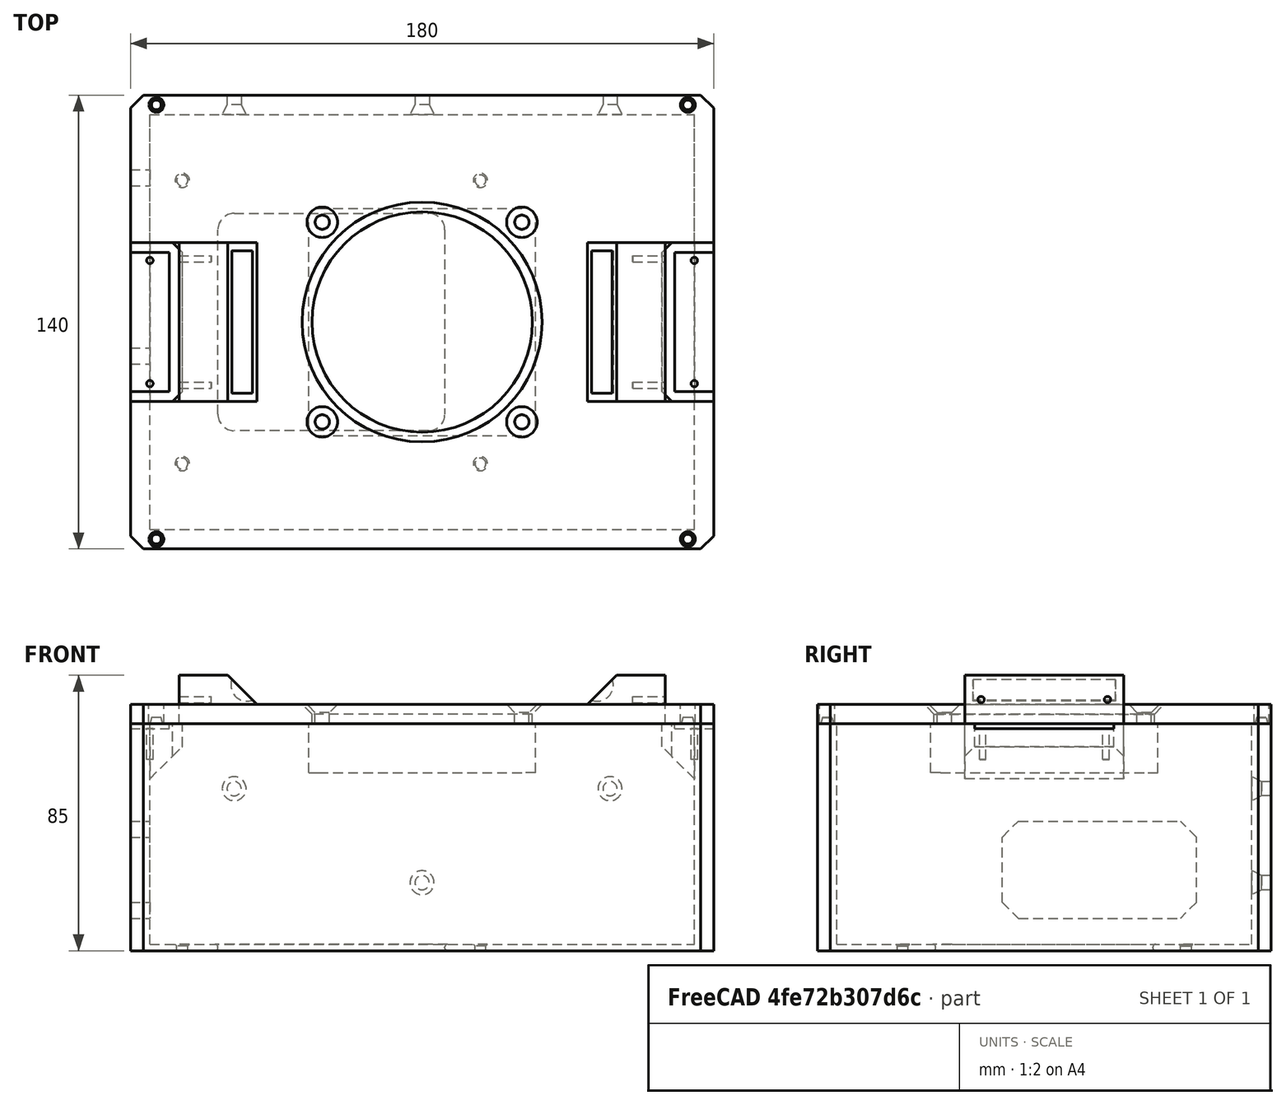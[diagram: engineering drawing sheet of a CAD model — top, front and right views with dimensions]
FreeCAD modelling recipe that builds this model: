
FCSTD DOCUMENT  (FreeCAD 0.19R24276 (Git))
Label: CajaElectronicaANETA8
License: All rights reserved
LicenseURL: http://en.wikipedia.org/wiki/All_rights_reserved
objects: Part::Cylinder×26, Part::MultiFuse×18, Part::Offset×15, TechDraw::DrawViewDimension×15, Part::Box×14, Part::Cut×13, Part::Chamfer×9, Part::Cone×7, Part::Fillet×3, TechDraw::DrawProjGroupItem×3, TechDraw::DrawSVGTemplate×2, TechDraw::DrawViewPart×2, TechDraw::DrawPage×2, TechDraw::DrawProjGroup×1, TechDraw::DrawViewAnnotation×1
note: 105 computed .brp shape members not serialized (recipe doc carries the construction recipe); baked Part::Feature solids carry a one-line shape summary decoded from their .brp

FEATURE [Part::Box] Box  label="Cubo"
  AttacherType = Attacher::AttachEngine3D
  Height = 70
  Length = 180
  Width = 140
FEATURE [Part::Box] Box001  label="Cubo001"
  AttacherType = Attacher::AttachEngine3D
  Height = 68
  Length = 168
  Placement = pos=(6,6,2) rot=(0,0,1;0rad)
  Width = 128
FEATURE [Part::Cut] Cut
  Base = -> Box
  Tool = -> Box001
FEATURE [Part::Cylinder] Cylinder  label="Cilindro"
  Angle = 360
  AttacherType = Attacher::AttachEngine3D
  Height = 2
  Placement = pos=(16,26.3,0) rot=(0,0,1;0rad)
  Radius = 1.5
FEATURE [Part::Cylinder] Cylinder001  label="Cilindro001"
  Angle = 360
  AttacherType = Attacher::AttachEngine3D
  Height = 2
  Placement = pos=(16,113.7,0) rot=(0,0,1;0rad)
  Radius = 1.5
FEATURE [Part::Cylinder] Cylinder002  label="Cilindro002"
  Angle = 360
  AttacherType = Attacher::AttachEngine3D
  Height = 2
  Placement = pos=(108,26.3,0) rot=(0,0,1;0rad)
  Radius = 1.5
FEATURE [Part::Cylinder] Cylinder003  label="Cilindro003"
  Angle = 360
  AttacherType = Attacher::AttachEngine3D
  Height = 2
  Placement = pos=(108,113.7,0) rot=(0,0,1;0rad)
  Radius = 1.5
FEATURE [Part::Chamfer] Chamfer
  Base = -> Cut
  Edges = 4 edges r=4: [Edge1,Edge3,Edge6,Edge15]
FEATURE [Part::Box] Box002  label="Cubo002"
  AttacherType = Attacher::AttachEngine3D
  Height = 2
  Length = 70
  Placement = pos=(27,36.5,0) rot=(0,0,1;0rad)
  Width = 67
FEATURE [Part::Fillet] Fillet
  Base = -> Box002
  Edges = 4 edges r=5: [Edge1,Edge3,Edge5,Edge7]
FEATURE [Part::Cut] Cut001
  Base = -> Chamfer
  Tool = -> Fillet
FEATURE [Part::Offset] Offset
  Fill = false
  Intersection = false
  Join = 0
  Mode = 0
  SelfIntersection = false
  Source = -> Cylinder
  Value = 0.2
FEATURE [Part::Offset] Offset001
  Fill = false
  Intersection = false
  Join = 0
  Mode = 0
  SelfIntersection = false
  Source = -> Cylinder001
  Value = 0.2
FEATURE [Part::Offset] Offset002
  Fill = false
  Intersection = false
  Join = 0
  Mode = 0
  SelfIntersection = false
  Source = -> Cylinder002
  Value = 0.2
FEATURE [Part::Offset] Offset003
  Fill = false
  Intersection = false
  Join = 0
  Mode = 0
  SelfIntersection = false
  Source = -> Cylinder003
  Value = 0.2
FEATURE [Part::MultiFuse] Fusion
  Shapes = -> [Offset,Offset001,Offset002,Offset003]
FEATURE [Part::Cut] Cut002
  Base = -> Cut001
  Tool = -> Fusion
FEATURE [Part::Chamfer] Chamfer001
  Base = -> Cut002
  Edges = 4 edges r=0.5: [Edge50,Edge52,Edge70,Edge72]
FEATURE [Part::Fillet] Fillet001
  Base = -> Chamfer001
  Edges = 2 edges r=0.9: [Edge17,Edge30]
FEATURE [Part::Cylinder] Cylinder004  label="Cilindro004"
  Angle = 360
  AttacherType = Attacher::AttachEngine3D
  Height = 6
  Placement = pos=(32,140,50) rot=(1,0,0;1.5708rad)
  Radius = 2
FEATURE [Part::Cylinder] Cylinder005  label="Cilindro005"
  Angle = 360
  AttacherType = Attacher::AttachEngine3D
  Height = 6
  Placement = pos=(148,140,50) rot=(1,0,0;1.5708rad)
  Radius = 2
FEATURE [Part::Cylinder] Cylinder006  label="Cilindro006"
  Angle = 360
  AttacherType = Attacher::AttachEngine3D
  Height = 6
  Placement = pos=(90,140,21) rot=(1,0,0;1.5708rad)
  Radius = 2
FEATURE [Part::Cone] Cone  label="Cono"
  Angle = 360
  AttacherType = Attacher::AttachEngine3D
  Height = 3
  Placement = pos=(90,137,21) rot=(1,0,0;1.5708rad)
  Radius1 = 2
  Radius2 = 3.5
FEATURE [Part::Cone] Cone001  label="Cono001"
  Angle = 360
  AttacherType = Attacher::AttachEngine3D
  Height = 3
  Placement = pos=(148,137,50) rot=(1,0,0;1.5708rad)
  Radius1 = 2
  Radius2 = 3.5
FEATURE [Part::Cone] Cone002  label="Cono002"
  Angle = 360
  AttacherType = Attacher::AttachEngine3D
  Height = 3
  Placement = pos=(32,137,50) rot=(1,0,0;1.5708rad)
  Radius1 = 2
  Radius2 = 3.5
FEATURE [Part::MultiFuse] Fusion001
  Shapes = -> [Cylinder004,Cone002]
FEATURE [Part::MultiFuse] Fusion002
  Shapes = -> [Cylinder005,Cone001]
FEATURE [Part::MultiFuse] Fusion003
  Shapes = -> [Cylinder006,Cone]
FEATURE [Part::Offset] Offset004
  Fill = false
  Intersection = false
  Join = 0
  Mode = 0
  SelfIntersection = false
  Source = -> Fusion001
  Value = 0.2
FEATURE [Part::Offset] Offset005
  Fill = false
  Intersection = false
  Join = 0
  Mode = 0
  SelfIntersection = false
  Source = -> Fusion002
  Value = 0.2
FEATURE [Part::Offset] Offset006
  Fill = false
  Intersection = false
  Join = 0
  Mode = 0
  SelfIntersection = false
  Source = -> Fusion003
  Value = 0.2
FEATURE [Part::MultiFuse] Fusion004
  Shapes = -> [Offset004,Offset005,Offset006]
FEATURE [Part::Cut] Cut003
  Base = -> Fillet001
  Tool = -> Fusion004
FEATURE [Part::Box] Box003  label="Cubo003"
  AttacherType = Attacher::AttachEngine3D
  Height = 30
  Length = 6
  Placement = pos=(0,57,10) rot=(0,0,1;0rad)
  Width = 60
FEATURE [Part::Chamfer] Chamfer002
  Base = -> Box003
  Edges = 4 edges r=5: [Edge9,Edge10,Edge11,Edge12]
FEATURE [Part::Cut] Cut004
  Base = -> Cut003
  Tool = -> Chamfer002
FEATURE [Part::Box] Box004  label="Cubo004"
  AttacherType = Attacher::AttachEngine3D
  Height = 1.5
  Length = 12
  Placement = pos=(0,48.5,68.5) rot=(0,0,1;0rad)
  Width = 43
FEATURE [Part::Box] Box005  label="Cubo005"
  AttacherType = Attacher::AttachEngine3D
  Height = 7
  Length = 16
  Placement = pos=(0,45.5,63) rot=(0,0,1;0rad)
  Width = 49
FEATURE [Part::Box] Box006  label="Cubo006"
  AttacherType = Attacher::AttachEngine3D
  Height = 1.5
  Length = 12
  Placement = pos=(168,48.5,68.5) rot=(0,0,1;0rad)
  Width = 43
FEATURE [Part::Box] Box007  label="Cubo007"
  AttacherType = Attacher::AttachEngine3D
  Height = 7
  Length = 16
  Placement = pos=(164,45.5,63) rot=(0,0,1;0rad)
  Width = 49
FEATURE [Part::MultiFuse] Fusion005
  Shapes = -> [Box005,Box007]
FEATURE [Part::MultiFuse] Fusion006
  Shapes = -> [Cut004,Fusion005]
FEATURE [Part::MultiFuse] Fusion007
  Shapes = -> [Box006,Box004]
FEATURE [Part::Cut] Cut005
  Base = -> Fusion006
  Tool = -> Fusion007
FEATURE [Part::Chamfer] Chamfer003
  Base = -> Cut005
  Edges = 2 edges r=9.99: [Edge165,Edge173]
FEATURE [Part::Cylinder] Cylinder007  label="Cilindro007"
  Angle = 360
  AttacherType = Attacher::AttachEngine3D
  Height = 10
  Placement = pos=(6,51,59) rot=(0,0,1;0rad)
  Radius = 1
FEATURE [Part::Cylinder] Cylinder008  label="Cilindro008"
  Angle = 360
  AttacherType = Attacher::AttachEngine3D
  Height = 10
  Placement = pos=(6,89,59) rot=(0,0,1;0rad)
  Radius = 1
FEATURE [Part::Cylinder] Cylinder009  label="Cilindro009"
  Angle = 360
  AttacherType = Attacher::AttachEngine3D
  Height = 10
  Placement = pos=(174,51,59) rot=(0,0,1;0rad)
  Radius = 1
FEATURE [Part::Cylinder] Cylinder010  label="Cilindro010"
  Angle = 360
  AttacherType = Attacher::AttachEngine3D
  Height = 10
  Placement = pos=(174,89,59) rot=(0,0,1;0rad)
  Radius = 1
FEATURE [Part::Box] Box008  label="Cubo008"
  AttacherType = Attacher::AttachEngine3D
  Height = 6
  Length = 180
  Placement = pos=(0,0,70) rot=(0,0,1;0rad)
  Width = 140
FEATURE [Part::Chamfer] Chamfer005
  Base = -> Box008
  Edges = 4 edges r=4: [Edge1,Edge3,Edge5,Edge7]
FEATURE [Part::Box] Box009  label="Cubo009"
  AttacherType = Attacher::AttachEngine3D
  Height = 15
  Length = 15
  Placement = pos=(0,45.5,70) rot=(0,0,1;0rad)
  Width = 49
FEATURE [Part::Box] Box010  label="Cubo010"
  AttacherType = Attacher::AttachEngine3D
  Height = 15
  Length = 15
  Placement = pos=(165,45.5,70) rot=(0,0,1;0rad)
  Width = 49
FEATURE [Part::Box] Box011  label="Cubo011"
  AttacherType = Attacher::AttachEngine3D
  Height = 15
  Length = 15
  Placement = pos=(15,45.5,70) rot=(0,0,1;0rad)
  Width = 49
FEATURE [Part::Box] Box012  label="Cubo012"
  AttacherType = Attacher::AttachEngine3D
  Height = 15
  Length = 15
  Placement = pos=(150,45.5,70) rot=(0,0,1;0rad)
  Width = 49
FEATURE [Part::MultiFuse] Fusion009
  Shapes = -> [Box009,Box010]
FEATURE [Part::Cut] Cut007
  Base = -> Chamfer005
  Tool = -> Fusion009
FEATURE [Part::MultiFuse] Fusion010
  Shapes = -> [Box011,Box012]
FEATURE [Part::MultiFuse] Fusion011
  Shapes = -> [Cut007,Fusion010]
FEATURE [Part::Chamfer] Chamfer006
  Base = -> Fusion011
  Edges = 2 edges r=8.99: [Edge7,Edge17]
FEATURE [Part::Cylinder] Cylinder011  label="Cilindro011"
  Angle = 360
  AttacherType = Attacher::AttachEngine3D
  Height = 10
  Placement = pos=(15,50.5,77.5) rot=(0,1,0;1.5708rad)
  Radius = 1
FEATURE [Part::Cylinder] Cylinder012  label="Cilindro012"
  Angle = 360
  AttacherType = Attacher::AttachEngine3D
  Height = 10
  Placement = pos=(15,89.5,77.5) rot=(0,1,0;1.5708rad)
  Radius = 1
FEATURE [Part::Cylinder] Cylinder013  label="Cilindro013"
  Angle = 360
  AttacherType = Attacher::AttachEngine3D
  Height = 10
  Placement = pos=(155,50.5,77.5) rot=(0,1,0;1.5708rad)
  Radius = 1
FEATURE [Part::Cylinder] Cylinder014  label="Cilindro014"
  Angle = 360
  AttacherType = Attacher::AttachEngine3D
  Height = 10
  Placement = pos=(155,89.5,77.5) rot=(0,1,0;1.5708rad)
  Radius = 1
FEATURE [Part::MultiFuse] Fusion012
  Shapes = -> [Cylinder011,Cylinder012,Cylinder013,Cylinder014]
FEATURE [Part::Cut] Cut008
  Base = -> Chamfer006
  Tool = -> Fusion012
FEATURE [Part::Cylinder] Cylinder015  label="Cilindro015"
  Angle = 360
  AttacherType = Attacher::AttachEngine3D
  Height = 44
  Placement = pos=(36,92,82) rot=(1,0,0;1.5708rad)
  Radius = 5
FEATURE [Part::Cylinder] Cylinder016  label="Cilindro016"
  Angle = 360
  AttacherType = Attacher::AttachEngine3D
  Height = 44
  Placement = pos=(144,92,82) rot=(1,0,0;1.5708rad)
  Radius = 5
FEATURE [Part::MultiFuse] Fusion013
  Shapes = -> [Cylinder015,Cylinder016]
FEATURE [Part::Cut] Cut009
  Base = -> Cut008
  Tool = -> Fusion013
FEATURE [Part::Cone] Cone007  label="Cono007"
  Angle = 360
  AttacherType = Attacher::AttachEngine3D
  Height = 2
  Placement = pos=(8,137,70) rot=(0,0,1;0rad)
  Radius1 = 2
  Radius2 = 1.5
FEATURE [Part::Cone] Cone008  label="Cono008"
  Angle = 360
  AttacherType = Attacher::AttachEngine3D
  Height = 2
  Placement = pos=(8,3,70) rot=(0,0,1;0rad)
  Radius1 = 2
  Radius2 = 1.5
FEATURE [Part::Cone] Cone009  label="Cono009"
  Angle = 360
  AttacherType = Attacher::AttachEngine3D
  Height = 2
  Placement = pos=(172,3,70) rot=(0,0,1;0rad)
  Radius1 = 2
  Radius2 = 1.5
FEATURE [Part::Cone] Cone010  label="Cono010"
  Angle = 360
  AttacherType = Attacher::AttachEngine3D
  Height = 2
  Placement = pos=(172,137,70) rot=(0,0,1;0rad)
  Radius1 = 2
  Radius2 = 1.5
FEATURE [Part::MultiFuse] Fusion015
  Shapes = -> [Cone008,Cone007,Cone010,Cone009]
FEATURE [Part::Cylinder] Cylinder017  label="Cilindro017"
  Angle = 360
  AttacherType = Attacher::AttachEngine3D
  Height = 6
  Placement = pos=(8,3,70) rot=(0,0,1;0rad)
  Radius = 2
FEATURE [Part::Cylinder] Cylinder018  label="Cilindro018"
  Angle = 360
  AttacherType = Attacher::AttachEngine3D
  Height = 6
  Placement = pos=(8,137,70) rot=(0,0,1;0rad)
  Radius = 2
FEATURE [Part::Cylinder] Cylinder019  label="Cilindro019"
  Angle = 360
  AttacherType = Attacher::AttachEngine3D
  Height = 6
  Placement = pos=(172,137,70) rot=(0,0,1;0rad)
  Radius = 2
FEATURE [Part::Cylinder] Cylinder020  label="Cilindro020"
  Angle = 360
  AttacherType = Attacher::AttachEngine3D
  Height = 6
  Placement = pos=(172,3,70) rot=(0,0,1;0rad)
  Radius = 2
FEATURE [Part::Offset] Offset007
  Fill = false
  Intersection = false
  Join = 0
  Mode = 0
  SelfIntersection = false
  Source = -> Cylinder017
  Value = 0.3
FEATURE [Part::Offset] Offset008
  Fill = false
  Intersection = false
  Join = 0
  Mode = 0
  SelfIntersection = false
  Source = -> Cylinder018
  Value = 0.3
FEATURE [Part::Offset] Offset009
  Fill = false
  Intersection = false
  Join = 0
  Mode = 0
  SelfIntersection = false
  Source = -> Cylinder019
  Value = 0.3
FEATURE [Part::Offset] Offset010
  Fill = false
  Intersection = false
  Join = 0
  Mode = 0
  SelfIntersection = false
  Source = -> Cylinder020
  Value = 0.3
FEATURE [Part::MultiFuse] Fusion017
  Shapes = -> [Offset007,Offset008,Offset009,Offset010]
FEATURE [Part::Cut] Cut010
  Base = -> Cut009
  Tool = -> Fusion017
FEATURE [Part::Box] Box013  label="Cubo013"
  AttacherType = Attacher::AttachEngine3D
  Height = 15
  Length = 70
  Placement = pos=(55,35,55) rot=(0,0,1;0rad)
  Width = 70
FEATURE [Part::Cylinder] Cylinder021  label="Cilindro021"
  Angle = 360
  AttacherType = Attacher::AttachEngine3D
  Height = 6
  Placement = pos=(90,70,70) rot=(0,0,1;0rad)
  Radius = 34
FEATURE [Part::Cut] Cut011
  Base = -> Cut010
  Tool = -> Cylinder021
FEATURE [Part::Fillet] Fillet002
  Base = -> Box013
  Edges = 4 edges r=3: [Edge1,Edge3,Edge5,Edge7]
FEATURE [Part::Cylinder] Cylinder022  label="Cilindro022"
  Angle = 360
  AttacherType = Attacher::AttachEngine3D
  Height = 6
  Placement = pos=(59.2,39.2,70) rot=(0,0,1;0rad)
  Radius = 2
FEATURE [Part::Cylinder] Cylinder023  label="Cilindro023"
  Angle = 360
  AttacherType = Attacher::AttachEngine3D
  Height = 6
  Placement = pos=(59.2,100.8,70) rot=(0,0,1;0rad)
  Radius = 2
FEATURE [Part::Cylinder] Cylinder024  label="Cilindro024"
  Angle = 360
  AttacherType = Attacher::AttachEngine3D
  Height = 6
  Placement = pos=(120.8,100.8,70) rot=(0,0,1;0rad)
  Radius = 2
FEATURE [Part::Cylinder] Cylinder025  label="Cilindro025"
  Angle = 360
  AttacherType = Attacher::AttachEngine3D
  Height = 6
  Placement = pos=(120.8,39.2,70) rot=(0,0,1;0rad)
  Radius = 2
FEATURE [Part::Offset] Offset011
  Fill = false
  Intersection = false
  Join = 0
  Mode = 0
  SelfIntersection = false
  Source = -> Cylinder022
  Value = 0.2
FEATURE [Part::Offset] Offset012
  Fill = false
  Intersection = false
  Join = 0
  Mode = 0
  SelfIntersection = false
  Source = -> Cylinder023
  Value = 0.2
FEATURE [Part::Offset] Offset013
  Fill = false
  Intersection = false
  Join = 0
  Mode = 0
  SelfIntersection = false
  Source = -> Cylinder024
  Value = 0.2
FEATURE [Part::Offset] Offset014
  Fill = false
  Intersection = false
  Join = 0
  Mode = 0
  SelfIntersection = false
  Source = -> Cylinder025
  Value = 0.2
FEATURE [Part::MultiFuse] Fusion018
  Shapes = -> [Offset011,Offset012,Offset013,Offset014]
FEATURE [Part::Cut] Cut012
  Base = -> Cut011
  Tool = -> Fusion018
FEATURE [Part::Chamfer] Chamfer007
  Base = -> Cut012
  Edges = 4 edges r=2.5: [Edge26,Edge28,Edge29,Edge30]
FEATURE [Part::Chamfer] Chamfer008
  Base = -> Chamfer007
  Edges = 1 edges r=3: [Edge27]
FEATURE [Part::MultiFuse] Fusion019
  Shapes = -> [Cylinder007,Cylinder008,Cylinder009,Cylinder010]
FEATURE [Part::Cut] Cut013
  Base = -> Chamfer003
  Tool = -> Fusion019
FEATURE [Part::Chamfer] Chamfer009
  Base = -> Cut013
  Edges = 4 edges r=3: [Edge21,Edge35,Edge198,Edge202]
FEATURE [Part::MultiFuse] Fusion020
  Shapes = -> [Fusion015,Chamfer009]
FEATURE [TechDraw::DrawSVGTemplate] Template
  EditableTexts = Designed_by_Name=<owner>; Drawing_number=001; FC-Date=-; FC-SC=3:1; FC-SH=1/2; FC-Title=A8ElectronicsBox; Subtitle=Caja Electronica A8; Weight=<500gr
  Height = 210
  Orientation = 1
  Width = 297
FEATURE [TechDraw::DrawSVGTemplate] Template001
  EditableTexts = Designed_by_Name=<owner>; Drawing_number=001; FC-Date=-; FC-SC=2/1; FC-SH=2/2; FC-Title=A8ElectronicsBox; Subtitle=Caja Electronica A8; Weight=<500gr
  Height = 210
  Orientation = 1
  Width = 297
FEATURE [TechDraw::DrawViewPart] View
  CoarseView = false
  Direction = (0.577,-0.577,0.577)
  Focus = 100
  HardHidden = false
  IsoCount = 0
  IsoHidden = false
  IsoVisible = false
  LockPosition = false
  Perspective = false
  Rotation = 0
  Scale = 0.5
  ScaleType = 0
  SeamHidden = false
  SeamVisible = true
  SmoothHidden = false
  SmoothVisible = true
  X = 216.292
  XDirection = (0.707,0.707,0)
  Y = 136.169
FEATURE [TechDraw::DrawProjGroupItem] ProjItem  label="Front"
  CoarseView = false
  Direction = (0,-1,0)
  Focus = 100
  HardHidden = false
  IsoCount = 0
  IsoHidden = false
  IsoVisible = false
  LockPosition = true
  Perspective = false
  Rotation = 0
  RotationVector = (1,0,0)
  Scale = 0.333333
  ScaleType = 2
  SeamHidden = false
  SeamVisible = true
  SmoothHidden = false
  SmoothVisible = true
  Type = 0
  X = 0
  XDirection = (1,0,0)
  Y = 0
FEATURE [TechDraw::DrawProjGroupItem] ProjItem001  label="Right"
  CoarseView = false
  Direction = (1,-1e-16,0)
  Focus = 100
  HardHidden = false
  IsoCount = 0
  IsoHidden = false
  IsoVisible = false
  LockPosition = false
  Perspective = false
  Rotation = 0
  RotationVector = (1,0,0)
  Scale = 0.333333
  ScaleType = 2
  SeamHidden = false
  SeamVisible = true
  SmoothHidden = false
  SmoothVisible = true
  Type = 2
  X = -68.3333
  XDirection = (1e-16,1,0)
  Y = 0
FEATURE [TechDraw::DrawProjGroupItem] ProjItem002  label="Top"
  CoarseView = false
  Direction = (0,0,1)
  Focus = 100
  HardHidden = false
  IsoCount = 0
  IsoHidden = false
  IsoVisible = false
  LockPosition = false
  Perspective = false
  Rotation = 0
  RotationVector = (1,0,0)
  Scale = 0.333333
  ScaleType = 2
  SeamHidden = false
  SeamVisible = true
  SmoothHidden = false
  SmoothVisible = true
  Type = 4
  X = 0
  XDirection = (1,0,0)
  Y = -61.6666
FEATURE [TechDraw::DrawProjGroup] ProjGroup
  Anchor = -> ProjItem
  AutoDistribute = true
  LockPosition = false
  ProjectionType = 0
  Rotation = 0
  Scale = 0.333333
  ScaleType = 2
  Views = -> [ProjItem,ProjItem001,ProjItem002]
  X = 111.097
  Y = 168.896
  spacingX = 15
  spacingY = 15
FEATURE [TechDraw::DrawViewPart] View001
  CoarseView = false
  Direction = (0.577,-0.577,0.577)
  Focus = 100
  HardHidden = false
  IsoCount = 0
  IsoHidden = false
  IsoVisible = false
  LockPosition = false
  Perspective = false
  Rotation = 0
  Scale = 0.5
  ScaleType = 0
  SeamHidden = false
  SeamVisible = true
  SmoothHidden = false
  SmoothVisible = true
  X = 152.584
  XDirection = (0.707,0.707,0)
  Y = 128.766
FEATURE [TechDraw::DrawViewDimension] Dimension
  Arbitrary = false
  ArbitraryTolerances = false
  EqualTolerance = true
  FormatSpec = %.2f
  FormatSpecOverTolerance = %+.2f
  FormatSpecUnderTolerance = %+.2f
  Inverted = false
  LockPosition = false
  MeasureType = 1
  OverTolerance = 0
  References2D = -> [ProjItem]
  Rotation = 0
  ScaleType = 0
  TheoreticalExact = false
  Type = 2
  UnderTolerance = 0
  X = 30
  Y = 1.47619
FEATURE [TechDraw::DrawViewDimension] Dimension001
  Arbitrary = false
  ArbitraryTolerances = false
  EqualTolerance = true
  FormatSpec = %.2f
  FormatSpecOverTolerance = %+.2f
  FormatSpecUnderTolerance = %+.2f
  Inverted = false
  LockPosition = false
  MeasureType = 1
  OverTolerance = 0
  References2D = -> [ProjItem]
  Rotation = 0
  ScaleType = 0
  TheoreticalExact = false
  Type = 1
  UnderTolerance = 0
  X = -1.62338
  Y = -16.8723
FEATURE [TechDraw::DrawViewDimension] Dimension002
  Arbitrary = false
  ArbitraryTolerances = false
  EqualTolerance = true
  FormatSpec = %.2f
  FormatSpecOverTolerance = %+.2f
  FormatSpecUnderTolerance = %+.2f
  Inverted = false
  LockPosition = false
  MeasureType = 1
  OverTolerance = 0
  References2D = -> [ProjItem002]
  Rotation = 0
  ScaleType = 0
  TheoreticalExact = false
  Type = 2
  UnderTolerance = 0
  X = -43.277
  Y = -0.270563
FEATURE [TechDraw::DrawPage] Page  label="Vistas"
  KeepUpdated = true
  NextBalloonIndex = 1
  ProjectionType = 0
  Template = -> Template
  Views = -> [View,ProjGroup,Dimension,Dimension001,Dimension002]
FEATURE [TechDraw::DrawViewDimension] Dimension003
  Arbitrary = false
  ArbitraryTolerances = false
  EqualTolerance = true
  FormatSpec = %.2f
  FormatSpecOverTolerance = %+.2f
  FormatSpecUnderTolerance = %+.2f
  Inverted = false
  LockPosition = false
  MeasureType = 1
  OverTolerance = 0
  References2D = -> [View001]
  Rotation = 0
  ScaleType = 0
  TheoreticalExact = false
  Type = 2
  UnderTolerance = 0
  X = -82.0227
  Y = 7.97225
FEATURE [TechDraw::DrawViewDimension] Dimension004
  Arbitrary = false
  ArbitraryTolerances = false
  EqualTolerance = true
  FormatSpec = %.2f
  FormatSpecOverTolerance = %+.2f
  FormatSpecUnderTolerance = %+.2f
  Inverted = false
  LockPosition = false
  MeasureType = 1
  OverTolerance = 0
  References2D = -> [View001]
  Rotation = 0
  ScaleType = 0
  TheoreticalExact = false
  Type = 0
  UnderTolerance = 0
  X = 20.975
  Y = -47.3568
FEATURE [TechDraw::DrawViewDimension] Dimension005
  Arbitrary = false
  ArbitraryTolerances = false
  EqualTolerance = true
  FormatSpec = %.2f
  FormatSpecOverTolerance = %+.2f
  FormatSpecUnderTolerance = %+.2f
  Inverted = false
  LockPosition = false
  MeasureType = 1
  OverTolerance = 0
  References2D = -> [View001]
  Rotation = 0
  ScaleType = 0
  TheoreticalExact = false
  Type = 0
  UnderTolerance = 0
  X = 38.5415
  Y = -15.4744
FEATURE [TechDraw::DrawViewDimension] Dimension006
  Arbitrary = false
  ArbitraryTolerances = false
  EqualTolerance = true
  FormatSpec = %.2f
  FormatSpecOverTolerance = %+.2f
  FormatSpecUnderTolerance = %+.2f
  Inverted = false
  LockPosition = false
  MeasureType = 1
  OverTolerance = 0
  References2D = -> [View001]
  Rotation = 0
  ScaleType = 0
  TheoreticalExact = false
  Type = 2
  UnderTolerance = 0
  X = 0.568492
  Y = -4.83871
FEATURE [TechDraw::DrawViewDimension] Dimension007
  Arbitrary = false
  ArbitraryTolerances = false
  EqualTolerance = true
  FormatSpec = ⌀%.2f
  FormatSpecOverTolerance = %+.2f
  FormatSpecUnderTolerance = %+.2f
  Inverted = false
  LockPosition = false
  MeasureType = 1
  OverTolerance = 0
  References2D = -> [View001]
  Rotation = 0
  ScaleType = 0
  TheoreticalExact = false
  Type = 5
  UnderTolerance = 0
  X = -3.38204
  Y = 17.8496
FEATURE [TechDraw::DrawViewDimension] Dimension008
  Arbitrary = false
  ArbitraryTolerances = false
  EqualTolerance = true
  FormatSpec = ⌀%.2f
  FormatSpecOverTolerance = %+.2f
  FormatSpecUnderTolerance = %+.2f
  Inverted = false
  LockPosition = false
  MeasureType = 1
  OverTolerance = 0
  References2D = -> [View001]
  Rotation = 0
  ScaleType = 0
  TheoreticalExact = false
  Type = 5
  UnderTolerance = 0
  X = 0.375782
  Y = 40.5844
FEATURE [TechDraw::DrawViewDimension] Dimension009
  Arbitrary = false
  ArbitraryTolerances = false
  EqualTolerance = true
  FormatSpec = ⌀%.2f
  FormatSpecOverTolerance = %+.2f
  FormatSpecUnderTolerance = %+.2f
  Inverted = false
  LockPosition = false
  MeasureType = 1
  OverTolerance = 0
  References2D = -> [View001]
  Rotation = 0
  ScaleType = 0
  TheoreticalExact = false
  Type = 5
  UnderTolerance = 0
  X = -12.1419
  Y = 44.943
FEATURE [TechDraw::DrawViewDimension] Dimension010
  Arbitrary = false
  ArbitraryTolerances = false
  EqualTolerance = true
  FormatSpec = %.2f
  FormatSpecOverTolerance = %+.2f
  FormatSpecUnderTolerance = %+.2f
  Inverted = false
  LockPosition = false
  MeasureType = 1
  OverTolerance = 0
  References2D = -> [View001]
  Rotation = 0
  ScaleType = 0
  TheoreticalExact = false
  Type = 0
  UnderTolerance = 0
  X = -39.544
  Y = 19.1135
FEATURE [TechDraw::DrawViewDimension] Dimension011
  Arbitrary = false
  ArbitraryTolerances = false
  EqualTolerance = true
  FormatSpec = %.2f
  FormatSpecOverTolerance = %+.2f
  FormatSpecUnderTolerance = %+.2f
  Inverted = false
  LockPosition = false
  MeasureType = 1
  OverTolerance = 0
  References2D = -> [View001]
  Rotation = 0
  ScaleType = 0
  TheoreticalExact = false
  Type = 0
  UnderTolerance = 0
  X = 30.097
  Y = 29.8493
FEATURE [TechDraw::DrawViewDimension] Dimension012
  Arbitrary = false
  ArbitraryTolerances = false
  EqualTolerance = true
  FormatSpec = ⌀%.2f
  FormatSpecOverTolerance = %+.2f
  FormatSpecUnderTolerance = %+.2f
  Inverted = false
  LockPosition = false
  MeasureType = 1
  OverTolerance = 0
  References2D = -> [View001]
  Rotation = 0
  ScaleType = 0
  TheoreticalExact = false
  Type = 5
  UnderTolerance = 0
  X = -48.6885
  Y = 11.6768
FEATURE [TechDraw::DrawViewDimension] Dimension013
  Arbitrary = false
  ArbitraryTolerances = false
  EqualTolerance = true
  FormatSpec = %.2f
  FormatSpecOverTolerance = %+.2f
  FormatSpecUnderTolerance = %+.2f
  Inverted = false
  LockPosition = false
  MeasureType = 1
  OverTolerance = 0
  References2D = -> [View001]
  Rotation = 0
  ScaleType = 0
  TheoreticalExact = false
  Type = 2
  UnderTolerance = 0
  X = 43.9836
  Y = 1.96191
FEATURE [TechDraw::DrawViewDimension] Dimension014
  Arbitrary = false
  ArbitraryTolerances = false
  EqualTolerance = true
  FormatSpec = %.2f
  FormatSpecOverTolerance = %+.2f
  FormatSpecUnderTolerance = %+.2f
  Inverted = false
  LockPosition = false
  MeasureType = 1
  OverTolerance = 0
  References2D = -> [View001]
  Rotation = 0
  ScaleType = 0
  TheoreticalExact = false
  Type = 0
  UnderTolerance = 0
  X = 17.7928
  Y = -11.3022
FEATURE [TechDraw::DrawViewAnnotation] Annotation
  Font = osifont
  LineSpace = 80
  LockPosition = false
  MaxWidth = -1
  Rotation = 0
  ScaleType = 0
  Text = Aproximate measurements: | Check with 3D piece
  TextSize = 5
  TextStyle = 0
  X = 60.9
  Y = 81
FEATURE [TechDraw::DrawPage] Page001  label="Cotas"
  KeepUpdated = true
  NextBalloonIndex = 1
  ProjectionType = 0
  Template = -> Template001
  Views = -> [View001,Dimension003,Dimension004,Dimension005,Dimension006,Dimension007,Dimension008,Dimension009,Dimension010,Dimension011,Dimension012,Dimension013,Dimension014,Annotation]
